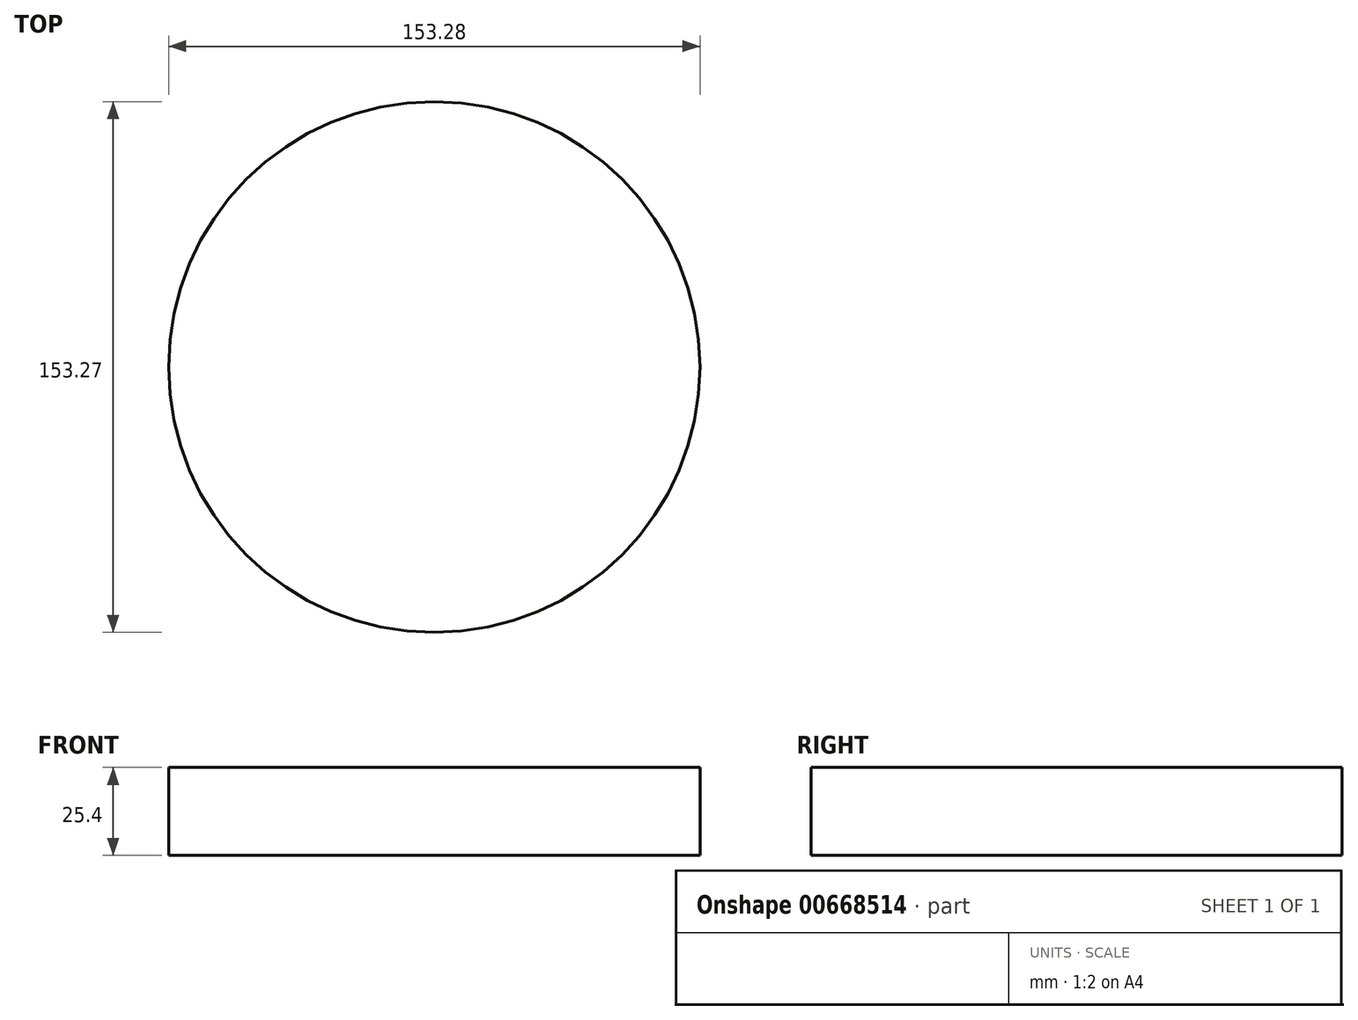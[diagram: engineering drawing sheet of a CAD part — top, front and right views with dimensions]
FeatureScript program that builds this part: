
annotation { "Feature Type Name" : "Feature", "Feature Type Description" : "" }
export const myFeature = defineFeature(function(context is Context, id is Id, definition is map)
    precondition{}
    {
        {
            var Q0;
            Q0=qCreatedBy(makeId("Top.planeOp"),FACE);
            var sketch = newSketch(context, id + "F0", { "sketchPlane" : qUnion([Q0])});
            skCircle(sketch, "E0", {"center": v(0, 36.59) * mm, "radius": 76.64 * mm});
            skSolve(sketch);
        }
        {
            var Q0;
            Q0=makeQuery(id+"F0.imprint","IMPRINT",FACE,{"disambiguationData":[TD([[makeQuery(id+"F0.imprint","IMPRINT",EDGE,{"derivedFrom":sQuery(id+"F0.wireOp",EDGE,"E0")}),1.0]])]});
            extrude(context, id + "F1", {"entities" : qUnion([Q0]), "depth" : 25.4 * mm, "offsetDistance" : 25.4 * mm});
        }
    });
